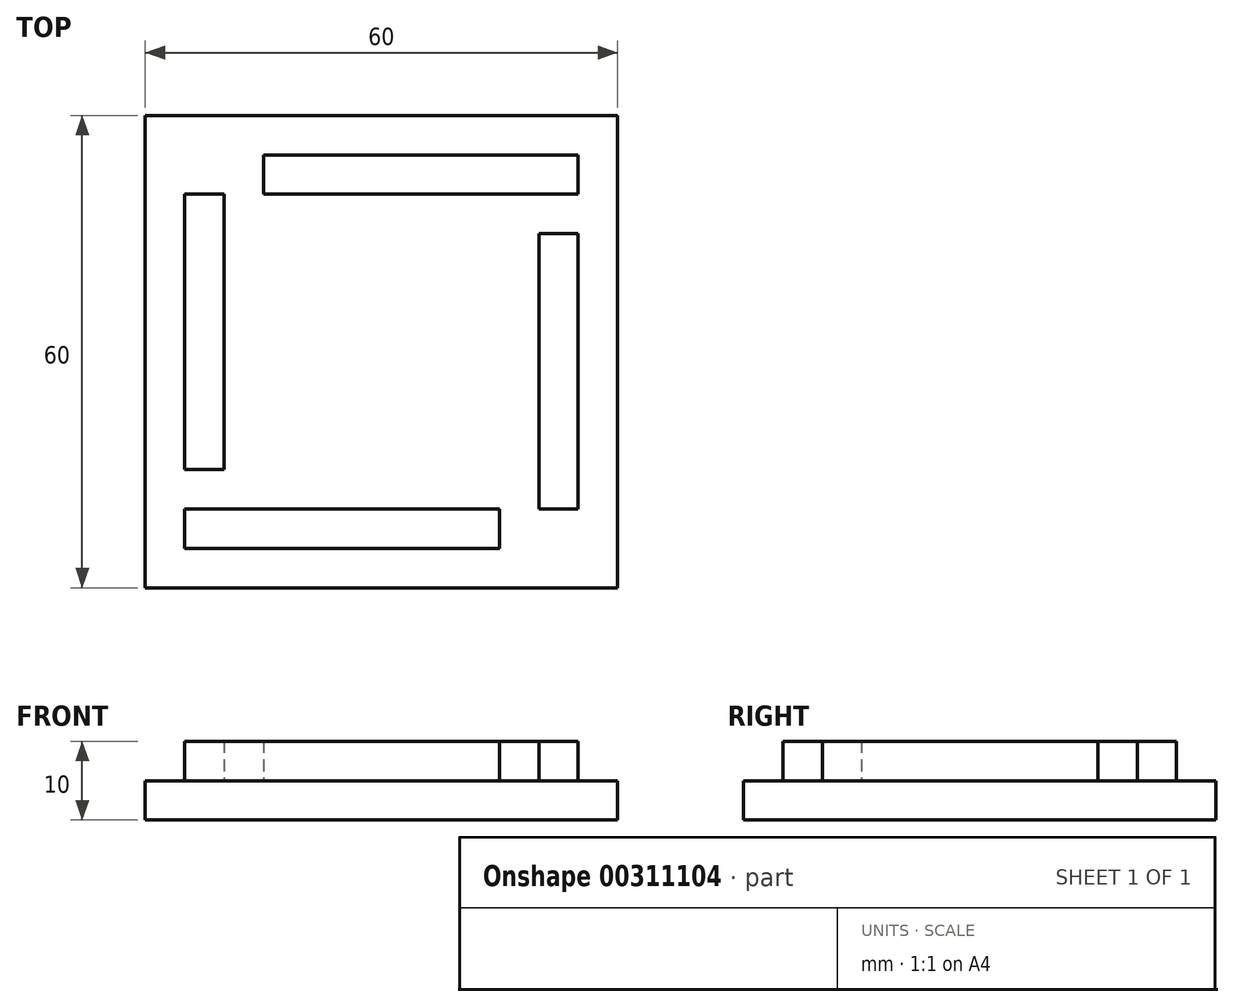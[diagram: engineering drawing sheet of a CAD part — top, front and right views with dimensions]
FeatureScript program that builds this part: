
annotation { "Feature Type Name" : "Feature", "Feature Type Description" : "" }
export const myFeature = defineFeature(function(context is Context, id is Id, definition is map)
    precondition{}
    {
        {
            var Q0;
            Q0=qCreatedBy(makeId("Top.planeOp"),FACE);
            var sketch = newSketch(context, id + "F0", { "sketchPlane" : qUnion([Q0])});
            skLineSegment(sketch, "E0.bottom", {"start": v(0, 0) * mm, "end": v(60, 0) * mm});
            skLineSegment(sketch, "E0.top", {"start": v(0, 60) * mm, "end": v(60, 60) * mm});
            skLineSegment(sketch, "E0.left", {"start": v(0, 0) * mm, "end": v(0, 60) * mm});
            skLineSegment(sketch, "E0.right", {"start": v(60, 0) * mm, "end": v(60, 60) * mm});
            skSolve(sketch);
        }
        {
            var Q0;
            Q0=makeQuery(id+"F0.imprint","IMPRINT",FACE,{"disambiguationData":[TD([[makeQuery(id+"F0.imprint","IMPRINT",EDGE,{"derivedFrom":sQuery(id+"F0.wireOp",EDGE,"E0.bottom")}),1.0]])]});
            extrude(context, id + "F1", {"entities" : qUnion([Q0]), "depth" : 5 * mm});
        }
        {
            var Q0;
            Q0=makeQuery(id+"F1.opExtrude","CAP_FACE",FACE,{"disambiguationData":[OSD([sQuery(id+"F0.wireOp",EDGE,"E0.bottom"),sQuery(id+"F0.wireOp",EDGE,"E0.top"),sQuery(id+"F0.wireOp",EDGE,"E0.left"),sQuery(id+"F0.wireOp",EDGE,"E0.right")])],"isStart":false});
            var sketch = newSketch(context, id + "F2", { "sketchPlane" : qUnion([Q0])});
            skLineSegment(sketch, "E1.bottom", {"start": v(5, 5) * mm, "end": v(45, 5) * mm});
            skLineSegment(sketch, "E1.top", {"start": v(5, 10) * mm, "end": v(45, 10) * mm});
            skLineSegment(sketch, "E1.left", {"start": v(5, 5) * mm, "end": v(5, 10) * mm});
            skLineSegment(sketch, "E1.right", {"start": v(45, 5) * mm, "end": v(45, 10) * mm});
            skLineSegment(sketch, "E2.bottom", {"start": v(50, 10) * mm, "end": v(55, 10) * mm});
            skLineSegment(sketch, "E2.top", {"start": v(50, 45) * mm, "end": v(55, 45) * mm});
            skLineSegment(sketch, "E2.left", {"start": v(50, 10) * mm, "end": v(50, 45) * mm});
            skLineSegment(sketch, "E2.right", {"start": v(55, 10) * mm, "end": v(55, 45) * mm});
            skLineSegment(sketch, "E3.bottom", {"start": v(55, 50) * mm, "end": v(15, 50) * mm});
            skLineSegment(sketch, "E3.left", {"start": v(55, 50) * mm, "end": v(55, 55) * mm});
            skLineSegment(sketch, "E3.right", {"start": v(15, 50) * mm, "end": v(15, 55) * mm});
            skLineSegment(sketch, "E4.bottom", {"start": v(5, 15) * mm, "end": v(10, 15) * mm});
            skLineSegment(sketch, "E4.left", {"start": v(5, 15) * mm, "end": v(5, 50) * mm});
            skLineSegment(sketch, "E4.right", {"start": v(10, 15) * mm, "end": v(10, 50) * mm});
            skLineSegment(sketch, "E5", {"start": v(5, 50) * mm, "end": v(10, 50) * mm});
            skLineSegment(sketch, "E6", {"start": v(15, 55) * mm, "end": v(55, 55) * mm});
            skSolve(sketch);
        }
        {
            var Q0;
            Q0=makeQuery(id+"F2.imprint","IMPRINT",FACE,{"disambiguationData":[TD([[makeQuery(id+"F2.imprint","IMPRINT",EDGE,{"derivedFrom":sQuery(id+"F2.wireOp",EDGE,"E1.bottom")}),1.0]])]});
            var Q1;
            Q1=makeQuery(id+"F2.imprint","IMPRINT",FACE,{"disambiguationData":[TD([[makeQuery(id+"F2.imprint","IMPRINT",EDGE,{"derivedFrom":sQuery(id+"F2.wireOp",EDGE,"E4.bottom")}),1.0]])]});
            var Q2;
            Q2=makeQuery(id+"F2.imprint","IMPRINT",FACE,{"disambiguationData":[TD([[makeQuery(id+"F2.imprint","IMPRINT",EDGE,{"derivedFrom":sQuery(id+"F2.wireOp",EDGE,"E3.bottom")}),-1.0]])]});
            var Q3;
            Q3=makeQuery(id+"F2.imprint","IMPRINT",FACE,{"disambiguationData":[TD([[makeQuery(id+"F2.imprint","IMPRINT",EDGE,{"derivedFrom":sQuery(id+"F2.wireOp",EDGE,"E2.bottom")}),1.0]])]});
            extrude(context, id + "F3", {"entities" : qUnion([Q0, Q1, Q2, Q3]), "operationType" : NewBodyOperationType.ADD, "depth" : 5 * mm});
        }
    });
